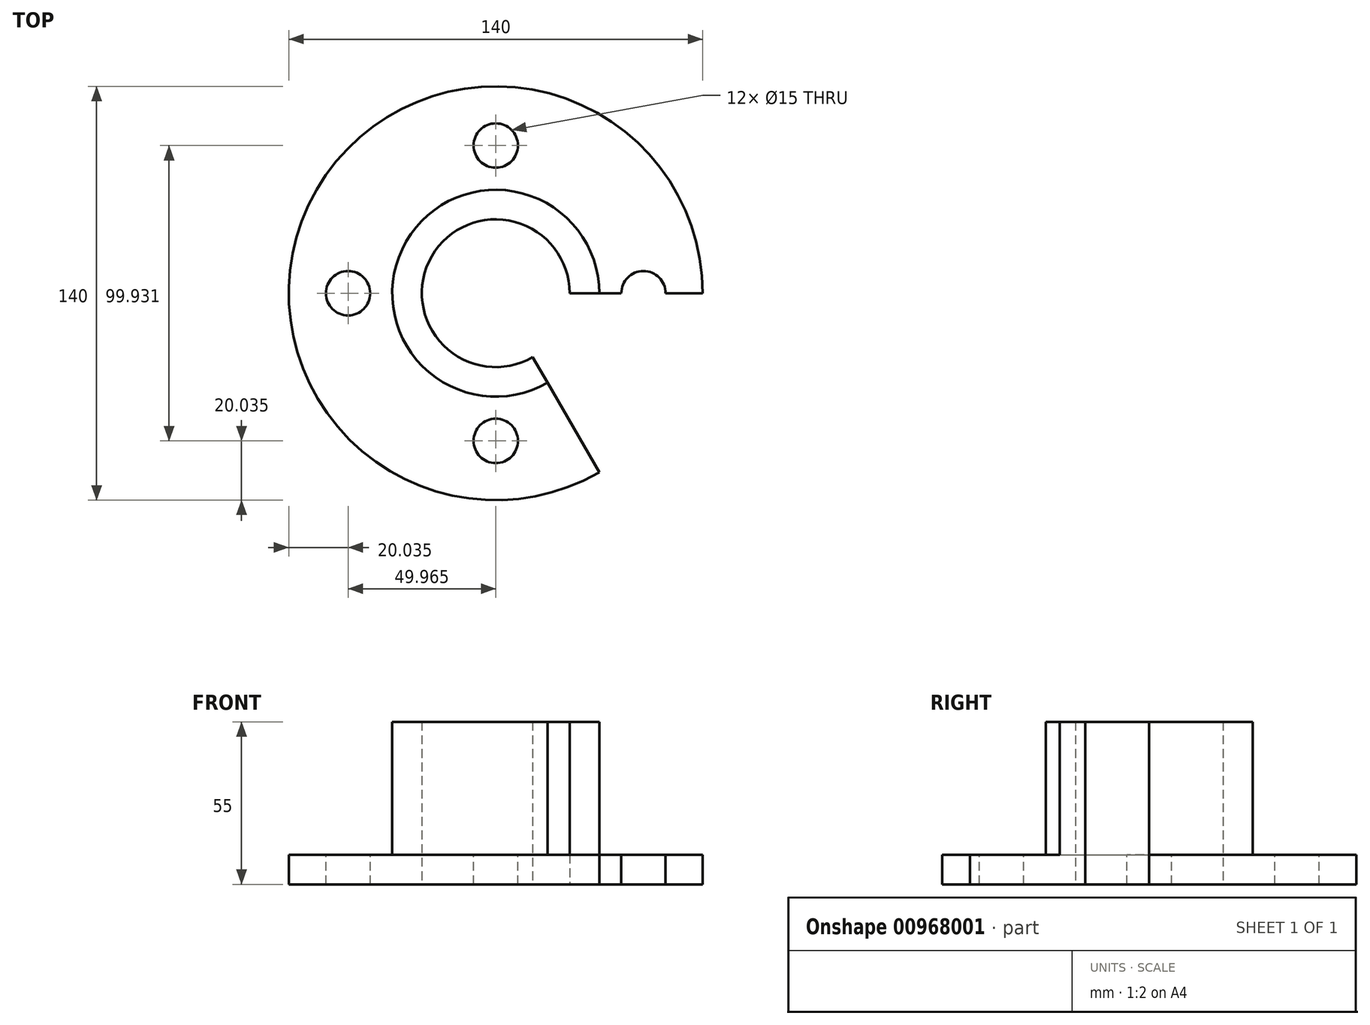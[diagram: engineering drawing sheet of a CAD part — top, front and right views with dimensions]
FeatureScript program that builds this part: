
annotation { "Feature Type Name" : "Feature", "Feature Type Description" : "" }
export const myFeature = defineFeature(function(context is Context, id is Id, definition is map)
    precondition{}
    {
        {
            var Q0;
            Q0=qCreatedBy(makeId("Front.planeOp"),FACE);
            var sketch = newSketch(context, id + "F0", { "sketchPlane" : qUnion([Q0])});
            skLineSegment(sketch, "E0", {"start": v(0, 0) * mm, "end": v(0, 60.3) * mm});
            skLineSegment(sketch, "E1", {"start": v(25, 55) * mm, "end": v(25, 0) * mm});
            skLineSegment(sketch, "E2", {"start": v(25, 0) * mm, "end": v(70, 0) * mm});
            skLineSegment(sketch, "E3", {"start": v(70, 0) * mm, "end": v(70, 10) * mm});
            skLineSegment(sketch, "E4", {"start": v(70, 10) * mm, "end": v(35, 10) * mm});
            skLineSegment(sketch, "E5", {"start": v(35, 10) * mm, "end": v(35, 55) * mm});
            skLineSegment(sketch, "E6", {"start": v(35, 55) * mm, "end": v(25, 55) * mm});
            skSolve(sketch);
        }
        {
            var Q0;
            Q0=makeQuery(id+"F0.imprint","IMPRINT",FACE,{"disambiguationData":[TD([[makeQuery(id+"F0.imprint","IMPRINT",EDGE,{"derivedFrom":sQuery(id+"F0.wireOp",EDGE,"E1")}),1.0]])]});
            var Q1;
            Q1=sQuery(id+"F0.wireOp",EDGE,"E0");
            revolve(context, id + "F1", {"surfaceOperationType" : NewSurfaceOperationType.NEW, "entities" : qUnion([Q0]), "axis" : qUnion([Q1]), "revolveType" : RevolveType.ONE_DIRECTION, "angle" : 300 * degree});
        }
        {
            var Q0;
            Q0=makeQuery(id+"F1.opRevolve","SWEPT_FACE",FACE,{"disambiguationData":[OSD([sQuery(id+"F0.wireOp",EDGE,"E4")])]});
            var sketch = newSketch(context, id + "F2", { "sketchPlane" : qUnion([Q0])});
            skCircle(sketch, "E7", {"center": v(-49.97, 0) * mm, "radius": 7.5 * mm});
            skCircle(sketch, "E8.1.0", {"center": v(0, -49.97) * mm, "radius": 7.5 * mm});
            skCircle(sketch, "E8.2.0", {"center": v(49.97, 0) * mm, "radius": 7.5 * mm});
            skCircle(sketch, "E8.3.0", {"center": v(0, 49.97) * mm, "radius": 7.5 * mm});
            skPoint(sketch, "E8.center", {"position": v(0, 0) * mm});
            skSolve(sketch);
        }
        {
            var Q0;
            {var subQ0=sQuery(id+"F2.wireOp",EDGE,"E8.2.0");var subQ1=makeQuery(id+"F1.opRevolve","CAP_EDGE",EDGE,{"disambiguationData":[OSD([sQuery(id+"F0.wireOp",EDGE,"E4")])],"isStart":true});var subQ2=makeQuery(id+"F2.imprint","INTERSECT",VERTEX,{"disambiguationData":[OD(0.0)],"derivedFrom":[subQ1,subQ0]});Q0=makeQuery(id+"F2.imprint","IMPRINT",FACE,{"disambiguationData":[TD([[makeQuery(id+"F2.imprint","IMPRINT",EDGE,{"disambiguationData":[TD([[subQ2,-1.0]])],"derivedFrom":subQ0}),1.0]])]});}
            var Q1;
            Q1=makeQuery(id+"F2.imprint","IMPRINT",FACE,{"disambiguationData":[TD([[makeQuery(id+"F2.imprint","IMPRINT",EDGE,{"derivedFrom":sQuery(id+"F2.wireOp",EDGE,"E8.3.0")}),1.0]])]});
            var Q2;
            Q2=makeQuery(id+"F2.imprint","IMPRINT",FACE,{"disambiguationData":[TD([[makeQuery(id+"F2.imprint","IMPRINT",EDGE,{"derivedFrom":sQuery(id+"F2.wireOp",EDGE,"E7")}),1.0]])]});
            var Q3;
            Q3=makeQuery(id+"F2.imprint","IMPRINT",FACE,{"disambiguationData":[TD([[makeQuery(id+"F2.imprint","IMPRINT",EDGE,{"derivedFrom":sQuery(id+"F2.wireOp",EDGE,"E8.1.0")}),1.0]])]});
            extrude(context, id + "F3", {"entities" : qUnion([Q0, Q1, Q2, Q3]), "operationType" : NewBodyOperationType.REMOVE, "endBound" : BoundingType.THROUGH_ALL, "oppositeDirection" : true, "depth" : 25 * mm, "offsetDistance" : 25 * mm});
        }
    });
